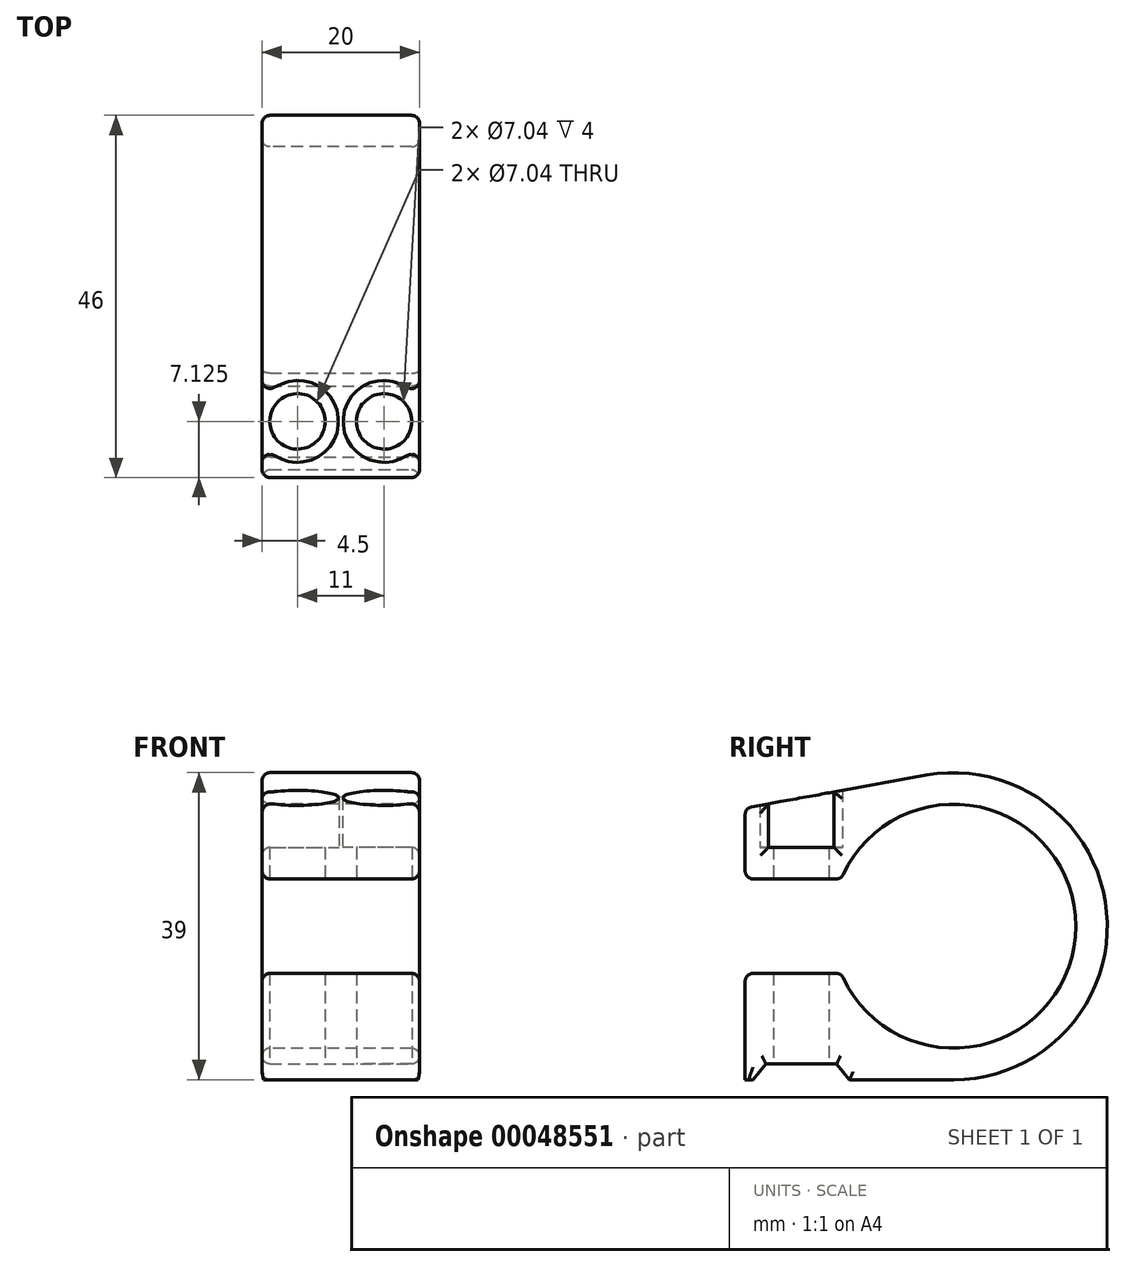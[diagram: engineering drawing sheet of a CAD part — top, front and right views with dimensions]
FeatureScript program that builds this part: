
annotation { "Feature Type Name" : "Feature", "Feature Type Description" : "" }
export const myFeature = defineFeature(function(context is Context, id is Id, definition is map)
    precondition{}
    {
        {
            var Q0;
            Q0=qCreatedBy(makeId("Right.planeOp"),FACE);
            var sketch = newSketch(context, id + "F0", { "sketchPlane" : qUnion([Q0])});
            skArc(sketch, "E0", {"start": v(-14.3, -6) * mm, "mid": v(15.5, 0) * mm, "end": v(-14.3, 6) * mm});
            skArc(sketch, "E1", {"start": v(-18.55, -6) * mm, "mid": v(16.73, -10) * mm, "end": v(-3.49, 19.19) * mm});
            skLineSegment(sketch, "E2", {"start": v(-14.3, 6) * mm, "end": v(-26.5, 6) * mm});
            skLineSegment(sketch, "E3", {"start": v(-26.5, 15) * mm, "end": v(-3.49, 19.19) * mm});
            skLineSegment(sketch, "E4", {"start": v(0, -19.5) * mm, "end": v(-26.5, -19.5) * mm});
            skLineSegment(sketch, "E5", {"start": v(-26.5, -19.5) * mm, "end": v(-26.5, -6) * mm});
            skLineSegment(sketch, "E6", {"start": v(-26.5, -6) * mm, "end": v(-14.3, -6) * mm});
            skPoint(sketch, "E7.start.orphan", {"position": v(-22.18, 0) * mm});
            skLineSegment(sketch, "E8", {"start": v(-26.5, 15) * mm, "end": v(-26.5, 6) * mm});
            skSolve(sketch);
        }
        {
            var Q0;
            {var subQ1=sQuery(id+"F0.wireOp",EDGE,"E7");Q0=makeQuery(id+"F0.imprint","IMPRINT",FACE,{"disambiguationData":[TD([[makeQuery(id+"F0.imprint","IMPRINT",EDGE,{"derivedFrom":subQ1}),-1.0]])]});}
            var Q1;
            {var subQ3=sQuery(id+"F0.wireOp",EDGE,"E0");Q1=makeQuery(id+"F0.imprint","IMPRINT",FACE,{"disambiguationData":[TD([[makeQuery(id+"F0.imprint","IMPRINT",EDGE,{"derivedFrom":subQ3}),-1.0]])]});}
            var Q2;
            {var subQ4=sQuery(id+"F0.wireOp",EDGE,"E4");Q2=makeQuery(id+"F0.imprint","IMPRINT",FACE,{"disambiguationData":[TD([[makeQuery(id+"F0.imprint","IMPRINT",EDGE,{"derivedFrom":subQ4}),-1.0]])]});}
            extrude(context, id + "F1", {"entities" : qUnion([Q0, Q1, Q2]), "endBound" : BoundingType.SYMMETRIC, "depth" : 20 * mm});
        }
        {
            var Q0;
            Q0=makeQuery(id+"F1.opExtrude","CAP_FACE",FACE,{"disambiguationData":[OSD([sQuery(id+"F0.wireOp",EDGE,"E0"),sQuery(id+"F0.wireOp",EDGE,"E1"),sQuery(id+"F0.wireOp",EDGE,"E2"),sQuery(id+"F0.wireOp",EDGE,"E7"),sQuery(id+"F0.wireOp",EDGE,"E3"),sQuery(id+"F0.wireOp",EDGE,"E4"),sQuery(id+"F0.wireOp",EDGE,"E5"),sQuery(id+"F0.wireOp",EDGE,"E6")])],"isStart":false});
            var sketch = newSketch(context, id + "F2", { "sketchPlane" : qUnion([Q0])});
            skLineSegment(sketch, "E9", {"start": v(-25.5, -19.5) * mm, "end": v(-23.88, -17.5) * mm});
            skLineSegment(sketch, "E10", {"start": v(-23.88, -17.5) * mm, "end": v(-14.88, -17.5) * mm});
            skPoint(sketch, "E11", {"position": v(-13.25, -19.5) * mm});
            skPoint(sketch, "E12.end.orphan", {"position": v(-15.5, -19.5) * mm});
            skLineSegment(sketch, "E13", {"start": v(-14.88, -17.5) * mm, "end": v(-13.25, -19.5) * mm});
            skSolve(sketch);
        }
        {
            var Q0;
            {var subQ2=sQuery(id+"F2.wireOp",EDGE,"E9");Q0=makeQuery(id+"F2.imprint","IMPRINT",FACE,{"disambiguationData":[TD([[makeQuery(id+"F2.imprint","IMPRINT",EDGE,{"derivedFrom":subQ2}),-1.0]])]});}
            extrude(context, id + "F3", {"entities" : qUnion([Q0]), "operationType" : NewBodyOperationType.REMOVE, "endBound" : BoundingType.UP_TO_NEXT, "oppositeDirection" : true, "depth" : 25 * mm});
        }
        {
            var Q0;
            Q0=makeQuery(id+"F1.opExtrude","SWEPT_FACE",FACE,{"disambiguationData":[OSD([sQuery(id+"F0.wireOp",EDGE,"E2")])]});
            var sketch = newSketch(context, id + "F4", { "sketchPlane" : qUnion([Q0])});
            skCircle(sketch, "E14", {"center": v(5.5, 19.38) * mm, "radius": 3.52 * mm});
            skCircle(sketch, "E15.MirrorC", {"center": v(-5.5, 19.38) * mm, "radius": 3.52 * mm});
            skSolve(sketch);
        }
        {
            var Q0;
            Q0 = qSketchRegion(id + "F4", true);
            extrude(context, id + "F5", {"entities" : qUnion([Q0]), "operationType" : NewBodyOperationType.REMOVE, "endBound" : BoundingType.SYMMETRIC, "oppositeDirection" : true, "depth" : 50 * mm});
        }
        {
            var Q0;
            Q0=makeQuery(id+"F1.opExtrude","SWEPT_FACE",FACE,{"disambiguationData":[OSD([sQuery(id+"F0.wireOp",EDGE,"E2")])]});
            var sketch = newSketch(context, id + "F6", { "sketchPlane" : qUnion([Q0])});
            skCircle(sketch, "E16", {"center": v(-5.5, 19.38) * mm, "radius": 5.25 * mm});
            skCircle(sketch, "E17.MirrorC", {"center": v(5.5, 19.38) * mm, "radius": 5.25 * mm});
            skSolve(sketch);
        }
        {
            var Q0;
            Q0=qCreatedBy(makeId("Top.planeOp"),FACE);
            cPlane(context, id + "F7", {"entities" : qUnion([Q0]), "cplaneType" : CPlaneType.OFFSET, "offset" : 10 * mm, "width" : 150 * mm, "height" : 150 * mm});
        }
        {
            var Q0;
            Q0=qCreatedBy(id+"F7.planeOp",FACE);
            var sketch = newSketch(context, id + "F8", { "sketchPlane" : qUnion([Q0])});
            skCircle(sketch, "E18", {"center": v(5.5, -19.38) * mm, "radius": 5.25 * mm});
            skCircle(sketch, "E19.MirrorC", {"center": v(-5.5, -19.38) * mm, "radius": 5.25 * mm});
            skSolve(sketch);
        }
        {
            var Q0;
            Q0 = qSketchRegion(id + "F8", true);
            extrude(context, id + "F9", {"entities" : qUnion([Q0]), "operationType" : NewBodyOperationType.REMOVE, "depth" : 25 * mm});
        }
        {
            var Q0;
            Q0=makeQuery(id+"F1.opExtrude","CAP_FACE",FACE,{"disambiguationData":[OSD([sQuery(id+"F0.wireOp",EDGE,"E0"),sQuery(id+"F0.wireOp",EDGE,"E1"),sQuery(id+"F0.wireOp",EDGE,"E2"),sQuery(id+"F0.wireOp",EDGE,"E3"),sQuery(id+"F0.wireOp",EDGE,"E4"),sQuery(id+"F0.wireOp",EDGE,"E5"),sQuery(id+"F0.wireOp",EDGE,"E6"),sQuery(id+"F0.wireOp",EDGE,"E8")])],"isStart":false});
            var Q1;
            Q1=makeQuery(id+"F1.opExtrude","CAP_FACE",FACE,{"disambiguationData":[OSD([sQuery(id+"F0.wireOp",EDGE,"E0"),sQuery(id+"F0.wireOp",EDGE,"E1"),sQuery(id+"F0.wireOp",EDGE,"E2"),sQuery(id+"F0.wireOp",EDGE,"E3"),sQuery(id+"F0.wireOp",EDGE,"E4"),sQuery(id+"F0.wireOp",EDGE,"E5"),sQuery(id+"F0.wireOp",EDGE,"E6"),sQuery(id+"F0.wireOp",EDGE,"E8")])],"isStart":true});
            var Q2;
            Q2=makeQuery(id+"F1.opExtrude","SWEPT_FACE",FACE,{"disambiguationData":[OSD([sQuery(id+"F0.wireOp",EDGE,"E8")])]});
            var Q3;
            Q3=makeQuery(id+"F1.opExtrude","SWEPT_EDGE",EDGE,{"disambiguationData":[OSD([sQuery(id+"F0.wireOp",EDGE,"E5"),sQuery(id+"F0.wireOp",EDGE,"E6")])]});
            var Q4;
            Q4=makeQuery(id+"F1.opExtrude","SWEPT_EDGE",EDGE,{"disambiguationData":[OSD([sQuery(id+"F0.wireOp",EDGE,"E0"),sQuery(id+"F0.wireOp",EDGE,"E6")])]});
            var Q5;
            Q5=makeQuery(id+"F1.opExtrude","SWEPT_EDGE",EDGE,{"disambiguationData":[OSD([sQuery(id+"F0.wireOp",EDGE,"E0"),sQuery(id+"F0.wireOp",EDGE,"E2")])]});
            fillet(context, id + "F10", {"entities" : qUnion([Q0, Q1, Q2, Q3, Q4, Q5]), "radius" : 1 * mm, "tangentPropagation" : true, "allowEdgeOverflow" : false});
        }
    });
